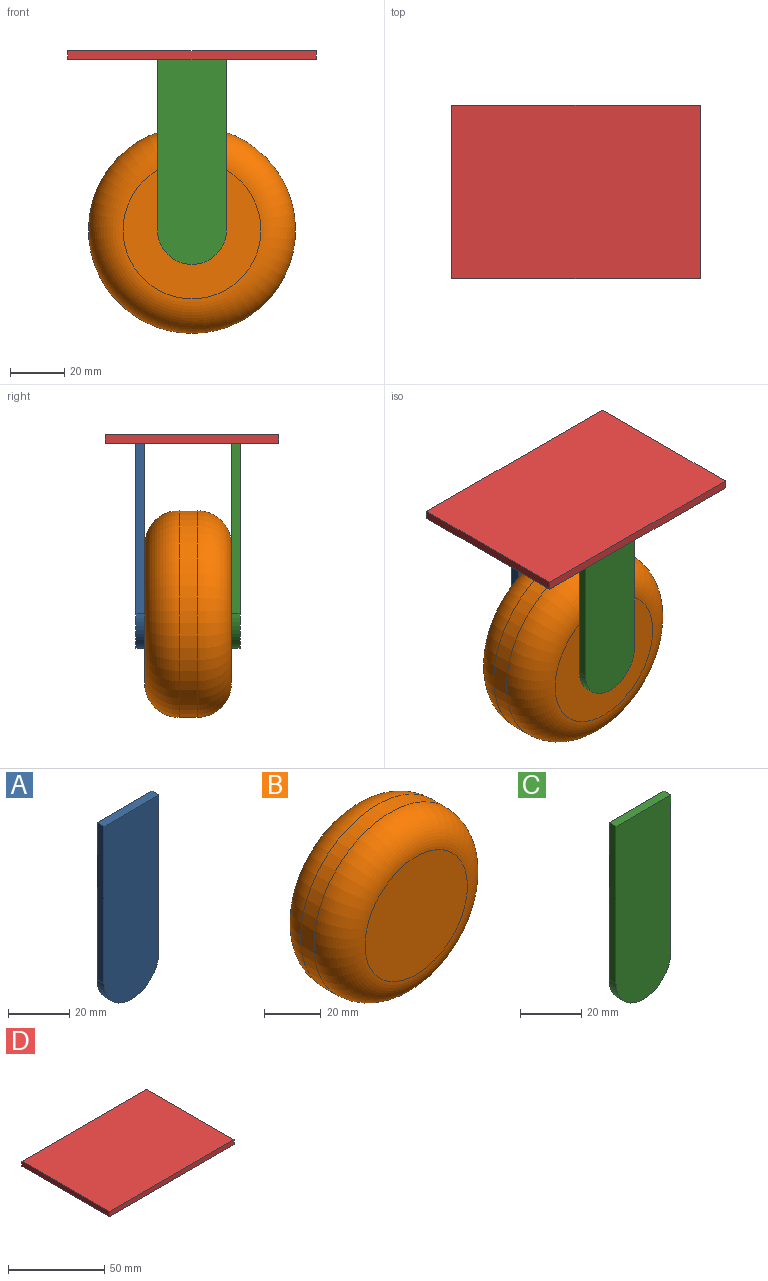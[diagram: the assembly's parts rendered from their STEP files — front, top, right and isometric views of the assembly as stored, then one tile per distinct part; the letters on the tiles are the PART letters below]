
ASSEMBLY  parts=4 mates=3
PART A: 6 faces, bbox 25.4x3.2x75.6 mm
  f0: plane 62.87x3.18mm, normal (1,0,0), area 199.6mm2, adj f1,f3,f4,f5
  f1: cylinder r=12.7mm len=25.4mm, axis (0,-1,0), area 126.7mm2, adj f0,f2,f4,f5
  f2: plane 62.87x3.18mm, normal (-1,0,0), area 199.6mm2, adj f1,f3,f4,f5
  f3: plane 25.4x3.18mm, normal (0,0,1), area 80.6mm2, adj f0,f2,f4,f5
  f4: plane 75.57x25.4mm, normal (0,1,0), area 1850.1mm2, adj f0,f1,f2,f3
  f5: plane 75.57x25.4mm, normal (0,-1,0), area 1850.1mm2, adj f0,f1,f2,f3
PART B: 5 faces, bbox 82.5x32x82.5 mm
  f0: cylinder r=38.1mm len=76.2mm, axis (0,1,0), area 1580.9mm2, adj f3,f4
  f1: plane 50.8x50.8mm, normal (0,-1,0), area 2026.8mm2, adj f4
  f2: plane 50.8x50.8mm, normal (0,1,0), area 2026.8mm2, adj f3
  f3: torus R=25.4mm, axis (0,-1,0), area 4197.2mm2, adj f0,f2
  f4: torus R=25.4mm, axis (0,-1,0), area 4197.2mm2, adj f0,f1
PART C: 6 faces, bbox 25.4x3.2x75.6 mm
  f0: plane 62.87x3.18mm, normal (1,0,0), area 199.6mm2, adj f1,f3,f4,f5
  f1: plane 25.4x3.18mm, normal (0,0,1), area 80.6mm2, adj f0,f2,f4,f5
  f2: plane 62.87x3.18mm, normal (-1,0,0), area 199.6mm2, adj f1,f3,f4,f5
  f3: cylinder r=12.7mm len=25.4mm, axis (0,1,0), area 126.7mm2, adj f0,f2,f4,f5
  f4: plane 75.57x25.4mm, normal (0,-1,0), area 1850.1mm2, adj f0,f1,f2,f3
  f5: plane 75.57x25.4mm, normal (0,1,0), area 1850.1mm2, adj f0,f1,f2,f3
PART D: 6 faces, bbox 91.4x64x3.2 mm
  f0: plane 91.44x3.18mm, normal (0,-1,0), area 290.3mm2, adj f1,f3,f4,f5
  f1: plane 64.01x3.18mm, normal (1,0,0), area 203.2mm2, adj f0,f2,f4,f5
  f2: plane 91.44x3.18mm, normal (0,1,0), area 290.3mm2, adj f1,f3,f4,f5
  f3: plane 64.01x3.18mm, normal (-1,0,0), area 203.2mm2, adj f0,f2,f4,f5
  f4: plane 91.44x64.01mm, normal (0,0,-1), area 5852.9mm2, adj f0,f1,f2,f3
  f5: plane 91.44x64.01mm, normal (0,0,1), area 5852.9mm2, adj f0,f1,f2,f3
PLACE A t=(-75.36,-9,25.12)mm
PLACE B t=(-75.36,-9,25.12)mm
PLACE C t=(-75.36,-9,25.12)mm
PLACE D t=(-75.36,-10.46,25.12)mm
MATE fastened D.f4 <-> A.f3  axis (0,0,-1) through (-75.36,-10.46,87.99)mm
MATE fastened B.f0 <-> C.f3  axis (0,-1,0) through (-75.36,-25,25.12)mm
MATE fastened B.f0 <-> A.f1  axis (0,1,0) through (-75.36,7,25.12)mm
